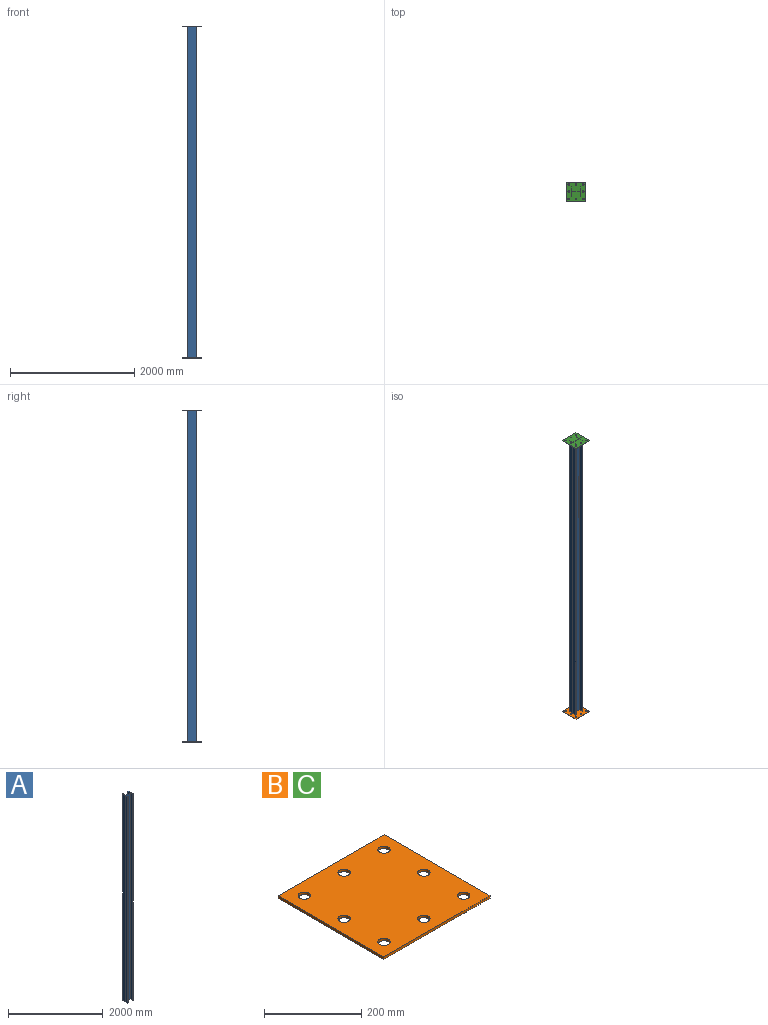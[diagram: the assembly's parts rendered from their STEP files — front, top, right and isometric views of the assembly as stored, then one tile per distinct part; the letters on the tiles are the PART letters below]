
ASSEMBLY  parts=3 mates=3
PART A: 14 faces, bbox 152.4x152.1x5321.3 mm
  f0: plane 152.4x152.15mm, normal (0,0,1), area 2822.7mm2, adj f1,f2,f3,f4,f5,f6,f7,f8
  f1: plane 5321.3x73.15mm, normal (1,0,0), area 389263.7mm2, adj f0,f2,f10,f12
  f2: plane 5321.3x139.19mm, normal (0,-1,0), area 740682.4mm2, adj f0,f1,f3,f10
  f3: plane 5321.3x73.15mm, normal (-1,0,0), area 389263.7mm2, adj f0,f2,f4,f10
  f4: plane 5321.3x6.6mm, normal (0,-1,0), area 35141.9mm2, adj f0,f3,f5,f10
  f5: plane 5321.3x152.15mm, normal (1,0,0), area 809614.5mm2, adj f0,f4,f6,f10
  f6: plane 5321.3x6.6mm, normal (0,1,0), area 35141.9mm2, adj f0,f5,f7,f10
  f7: plane 5321.3x73.15mm, normal (-1,0,0), area 389263.7mm2, adj f0,f6,f8,f10
  f8: plane 5321.3x139.19mm, normal (0,1,0), area 740682.4mm2, adj f0,f7,f9,f10
  f9: plane 5321.3x73.15mm, normal (1,0,0), area 389263.7mm2, adj f0,f8,f10,f11
  f10: plane 152.4x152.15mm, normal (0,0,-1), area 2822.7mm2, adj f1,f2,f3,f4,f5,f6,f7,f8
  f11: plane 5321.3x6.6mm, normal (0,1,0), area 35141.9mm2, adj f0,f9,f10,f13
  f12: plane 5321.3x6.6mm, normal (0,-1,0), area 35141.9mm2, adj f0,f1,f10,f13
  f13: plane 5321.3x152.15mm, normal (-1,0,0), area 809614.5mm2, adj f0,f10,f11,f12
PART B: 14 faces, bbox 308.2x308.2x6.4 mm
  f0: plane 308.22x308.22mm, normal (0,0,1), area 90943.6mm2, adj f1,f3,f4,f5,f6,f7,f8,f9
  f1: plane 308.22x6.35mm, normal (-1,0,0), area 1957.2mm2, adj f0,f2,f3,f4
  f2: plane 308.22x308.22mm, normal (0,0,-1), area 90943.6mm2, adj f1,f3,f4,f5,f6,f7,f8,f9
  f3: plane 308.22x6.35mm, normal (0,-1,0), area 1957.2mm2, adj f0,f1,f2,f5
  f4: plane 308.22x6.35mm, normal (0,1,0), area 1957.2mm2, adj f0,f1,f2,f5
  f5: plane 308.22x6.35mm, normal (1,0,0), area 1957.2mm2, adj f0,f2,f3,f4
  f6: cylinder r=12.7mm len=25.4mm, axis (0,0,-1), area 506.7mm2, adj f0,f2
  f7: cylinder r=12.7mm len=25.4mm, axis (0,0,-1), area 506.7mm2, adj f0,f2
  f8: cylinder r=12.7mm len=25.4mm, axis (0,0,-1), area 506.7mm2, adj f0,f2
  f9: cylinder r=12.7mm len=25.4mm, axis (0,0,-1), area 506.7mm2, adj f0,f2
  f10: cylinder r=12.7mm len=25.4mm, axis (0,0,-1), area 506.7mm2, adj f0,f2
  f11: cylinder r=12.7mm len=25.4mm, axis (0,0,-1), area 506.7mm2, adj f0,f2
  f12: cylinder r=12.7mm len=25.4mm, axis (0,0,-1), area 506.7mm2, adj f0,f2
  f13: cylinder r=12.7mm len=25.4mm, axis (0,0,-1), area 506.7mm2, adj f0,f2
PART C: same geometry as B
PLACE A t=(319.67,-3419.44,2578.93)mm
PLACE B t=(319.67,-3419.44,2578.93)mm
PLACE C t=(319.67,-3419.44,7906.58)mm
MATE planar B.f0 <-> A.f10  axis (0,0,1) through (-2960.91,-179.98,-5563.99)mm
MATE slider C.f2 <-> B.f0  axis (0,0,-1) through (-2960.91,-179.98,-242.69)mm
MATE fastened C.f2 <-> A.f0  axis (0,0,-1) through (-2960.91,-179.98,-242.69)mm
